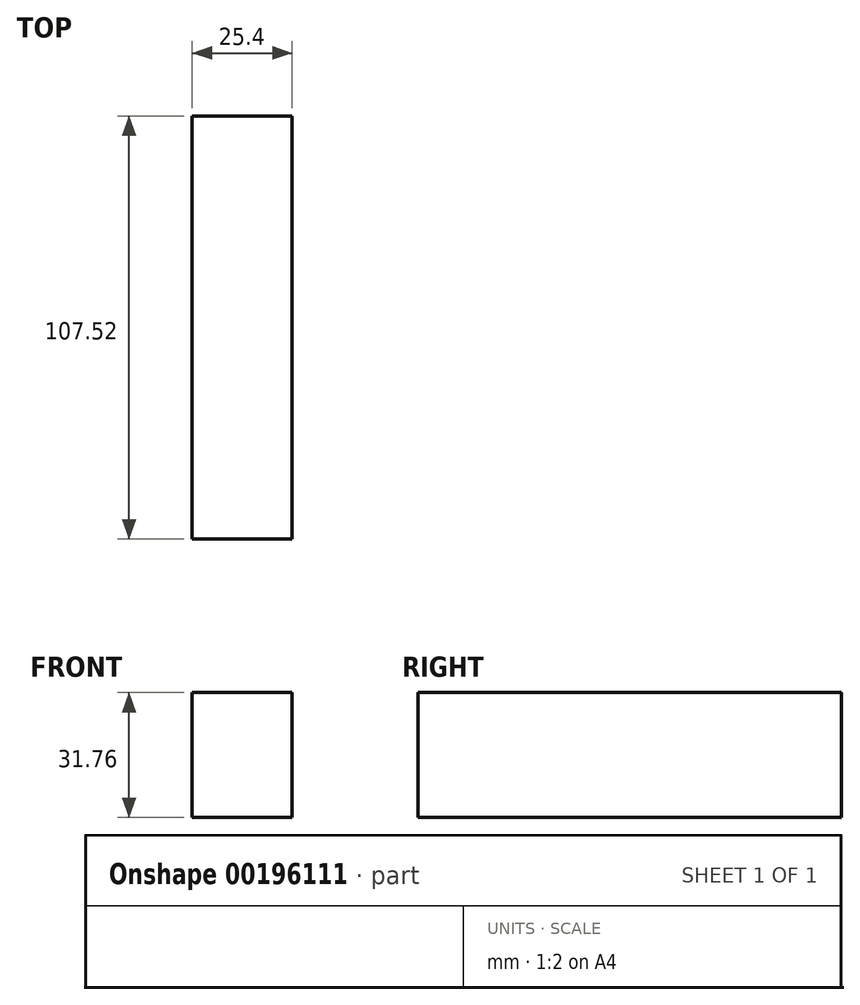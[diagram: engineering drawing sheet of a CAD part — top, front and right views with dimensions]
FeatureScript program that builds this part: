
annotation { "Feature Type Name" : "Feature", "Feature Type Description" : "" }
export const myFeature = defineFeature(function(context is Context, id is Id, definition is map)
    precondition{}
    {
        {
            var Q0;
            Q0=qCreatedBy(makeId("Right.planeOp"),FACE);
            var sketch = newSketch(context, id + "F0", { "sketchPlane" : qUnion([Q0])});
            skLineSegment(sketch, "E0.bottom", {"start": v(-53.76, 15.88) * mm, "end": v(53.76, 15.88) * mm});
            skLineSegment(sketch, "E0.top", {"start": v(-53.76, -15.88) * mm, "end": v(53.76, -15.88) * mm});
            skLineSegment(sketch, "E0.left", {"start": v(-53.76, 15.88) * mm, "end": v(-53.76, -15.88) * mm});
            skLineSegment(sketch, "E0.right", {"start": v(53.76, 15.88) * mm, "end": v(53.76, -15.88) * mm});
            skPoint(sketch, "E0.middle", {"position": v(0, 0) * mm});
            skSolve(sketch);
        }
        {
            var Q0;
            Q0=makeQuery(id+"F0.imprint","IMPRINT",FACE,{"disambiguationData":[TD([[makeQuery(id+"F0.imprint","IMPRINT",EDGE,{"derivedFrom":sQuery(id+"F0.wireOp",EDGE,"E0.bottom")}),-1.0]])]});
            extrude(context, id + "F1", {"entities" : qUnion([Q0]), "depth" : 25.4 * mm});
        }
    });
